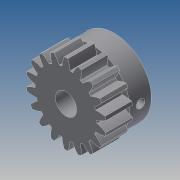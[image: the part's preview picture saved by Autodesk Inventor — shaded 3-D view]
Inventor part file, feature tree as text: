
AUTODESK INVENTOR PART (.ipt)
format: ipt  version: 2017 (Build 210142000, 142)  size: 260,096 bytes
history: native  units: mm
features: extrude x4, other x3, sketch x3, projected_geometry x1
ambient origin geometry x8: Origin, YZ Plane, XZ Plane, XY Plane, X Axis, Y Axis, Z Axis, Center Point
bodies: Body1 (feature_tree)
feature tree (11):
  other  "Sólido1"
  extrude  "Extrusión1"  Depth=10.0mm
  sketch  "Boceto2"  dims[d3=5.0mm d4=3.0mm]
  extrude  "Extrusión2"  Depth=3.0mm
  extrude  "Extrusión3"  Depth=10.0mm
  extrude  "Extrusión4"  TaperAngle=120.0deg  [1 undecoded]
  other  "Dientes de engranaje recto3"
  sketch  "Boceto1"  dims[d0=8.0mm d2=10.0mm]
  projected_geometry  "Contorno proyectado1"
  sketch  "Boceto3"  dims[d5=8.0mm d6=0.0mm d7=3.2mm d8=120.0deg d9=2.95mm d10=15.0mm d11=0.0mm d12=4.0mm d13=0.0mm d14=10.0mm d15=0.0mm]
  other  "iFeature1:3"
note: 1 required parameter value undecoded (feature->parameter linkage not recoverable at this tier; creation-order binding heuristic only, values carry confidence <= 0.55)
